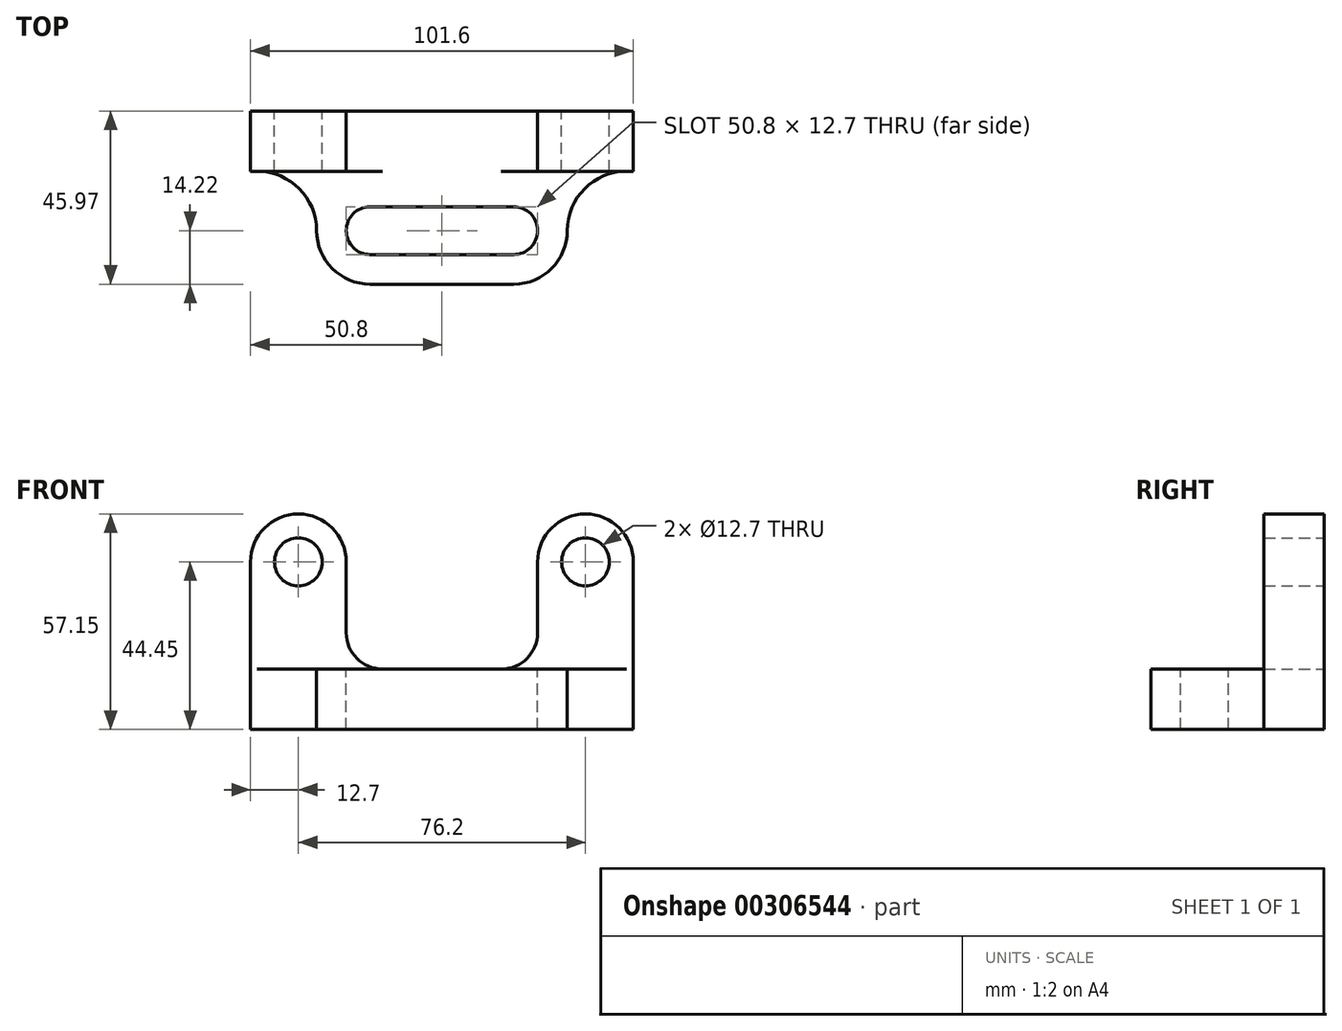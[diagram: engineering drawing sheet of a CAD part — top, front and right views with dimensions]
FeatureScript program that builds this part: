
annotation { "Feature Type Name" : "Feature", "Feature Type Description" : "" }
export const myFeature = defineFeature(function(context is Context, id is Id, definition is map)
    precondition{}
    {
        {
            var Q0;
            Q0=qCreatedBy(makeId("Front.planeOp"),FACE);
            var sketch = newSketch(context, id + "F0", { "sketchPlane" : qUnion([Q0])});
            skCircle(sketch, "E0", {"center": v(12.7, 44.45) * mm, "radius": 6.35 * mm});
            skCircle(sketch, "E1", {"center": v(88.9, 44.45) * mm, "radius": 6.35 * mm});
            skLineSegment(sketch, "E2", {"start": v(101.6, 44.45) * mm, "end": v(101.6, 0) * mm});
            skLineSegment(sketch, "E3", {"start": v(0, 44.45) * mm, "end": v(0, 0) * mm});
            skLineSegment(sketch, "E4", {"start": v(50.8, 0) * mm, "end": v(50.8, 24.18) * mm, "construction": true});
            skLineSegment(sketch, "E5", {"start": v(12.7, 44.45) * mm, "end": v(12.7, 34.07) * mm, "construction": true});
            skLineSegment(sketch, "E6", {"start": v(88.9, 44.45) * mm, "end": v(88.9, 31.32) * mm, "construction": true});
            skArc(sketch, "E7", {"start": v(0, 44.45) * mm, "mid": v(12.7, 57.15) * mm, "end": v(25.4, 44.45) * mm});
            skLineSegment(sketch, "E8", {"start": v(25.4, 44.45) * mm, "end": v(25.4, 25.65) * mm});
            skArc(sketch, "E9", {"start": v(25.4, 25.65) * mm, "mid": v(28.23, 18.83) * mm, "end": v(35.05, 16) * mm});
            skLineSegment(sketch, "E10", {"start": v(35.05, 16) * mm, "end": v(66.55, 16) * mm});
            skArc(sketch, "E11", {"start": v(66.55, 16) * mm, "mid": v(73.37, 18.83) * mm, "end": v(76.2, 25.65) * mm});
            skLineSegment(sketch, "E12", {"start": v(76.2, 25.65) * mm, "end": v(76.2, 44.45) * mm});
            skArc(sketch, "E13", {"start": v(101.6, 44.45) * mm, "mid": v(88.9, 57.15) * mm, "end": v(76.2, 44.45) * mm});
            skLineSegment(sketch, "E14", {"start": v(66.55, 16) * mm, "end": v(66.55, 22.94) * mm, "construction": true});
            skLineSegment(sketch, "E15", {"start": v(35.05, 16) * mm, "end": v(35.05, 31.62) * mm, "construction": true});
            skLineSegment(sketch, "E16", {"start": v(0, 0) * mm, "end": v(101.6, 0) * mm});
            skSolve(sketch);
        }
        {
            var Q0;
            Q0 = qSketchRegion(id + "F0", true);
            extrude(context, id + "F1", {"entities" : qUnion([Q0]), "depth" : 16 * mm});
        }
        {
            var Q0;
            Q0=makeQuery(id+"F1.opExtrude","CAP_FACE",FACE,{"disambiguationData":[OSD([sQuery(id+"F0.wireOp",EDGE,"E0"),sQuery(id+"F0.wireOp",EDGE,"E1"),sQuery(id+"F0.wireOp",EDGE,"E2"),sQuery(id+"F0.wireOp",EDGE,"E3"),sQuery(id+"F0.wireOp",EDGE,"E7"),sQuery(id+"F0.wireOp",EDGE,"E8"),sQuery(id+"F0.wireOp",EDGE,"E9"),sQuery(id+"F0.wireOp",EDGE,"E10"),sQuery(id+"F0.wireOp",EDGE,"E11"),sQuery(id+"F0.wireOp",EDGE,"E12"),sQuery(id+"F0.wireOp",EDGE,"E13"),sQuery(id+"F0.wireOp",EDGE,"E16")])],"isStart":false});
            var sketch = newSketch(context, id + "F2", { "sketchPlane" : qUnion([Q0])});
            skLineSegment(sketch, "E17.bottom", {"start": v(0, 0) * mm, "end": v(101.6, 0) * mm});
            skLineSegment(sketch, "E17.top", {"start": v(0, 16) * mm, "end": v(101.6, 16) * mm});
            skLineSegment(sketch, "E17.left", {"start": v(0, 0) * mm, "end": v(0, 16) * mm});
            skLineSegment(sketch, "E17.right", {"start": v(101.6, 0) * mm, "end": v(101.6, 16) * mm});
            skSolve(sketch);
        }
        {
            var Q0;
            Q0 = qSketchRegion(id + "F2", true);
            extrude(context, id + "F3", {"entities" : qUnion([Q0]), "operationType" : NewBodyOperationType.ADD, "depth" : 50.8 * mm});
        }
        {
            var Q0;
            Q0=makeQuery(id+"F3.boolean.opBoolean","MERGE",FACE,{"derivedFrom":[makeQuery(id+"F1.opExtrude","SWEPT_FACE",FACE,{"disambiguationData":[OSD([sQuery(id+"F0.wireOp",EDGE,"E10")])]}),makeQuery(id+"F3.opExtrude","SWEPT_FACE",FACE,{"disambiguationData":[OSD([sQuery(id+"F2.wireOp",EDGE,"E17.top")])]})]});
            var sketch = newSketch(context, id + "F4", { "sketchPlane" : qUnion([Q0])});
            skLineSegment(sketch, "E18", {"start": v(31.75, -31.75) * mm, "end": v(31.75, -19.05) * mm, "construction": true});
            skLineSegment(sketch, "E19", {"start": v(69.85, -31.75) * mm, "end": v(69.85, -21.92) * mm, "construction": true});
            skLineSegment(sketch, "E20", {"start": v(50.8, 0) * mm, "end": v(50.8, -10.67) * mm, "construction": true});
            skPoint(sketch, "E20.endSnap0", {"position": v(50.8, 0) * mm});
            skArc(sketch, "E21", {"start": v(17.53, -31.75) * mm, "mid": v(21.7, -41.8) * mm, "end": v(31.75, -45.97) * mm});
            skArc(sketch, "E22", {"start": v(84.07, -31.75) * mm, "mid": v(79.9, -41.8) * mm, "end": v(69.85, -45.97) * mm});
            skLineSegment(sketch, "E23", {"start": v(31.75, -45.97) * mm, "end": v(69.85, -45.97) * mm});
            skArc(sketch, "E24", {"start": v(17.53, -31.75) * mm, "mid": v(12.91, -20.61) * mm, "end": v(1.78, -16) * mm});
            skArc(sketch, "E25", {"start": v(84.07, -31.75) * mm, "mid": v(88.69, -20.61) * mm, "end": v(99.82, -16) * mm});
            skLineSegment(sketch, "E26", {"start": v(1.78, -16) * mm, "end": v(0, -16) * mm});
            skLineSegment(sketch, "E27", {"start": v(0, -16) * mm, "end": v(0, -66.8) * mm});
            skLineSegment(sketch, "E28", {"start": v(0, -66.8) * mm, "end": v(101.6, -66.8) * mm});
            skLineSegment(sketch, "E29", {"start": v(101.6, -66.8) * mm, "end": v(101.6, -16) * mm});
            skLineSegment(sketch, "E30", {"start": v(101.6, -16) * mm, "end": v(99.82, -16) * mm});
            skArc(sketch, "E31", {"start": v(31.75, -25.4) * mm, "mid": v(25.4, -31.75) * mm, "end": v(31.75, -38.1) * mm});
            skArc(sketch, "E32", {"start": v(69.85, -38.1) * mm, "mid": v(76.2, -31.75) * mm, "end": v(69.85, -25.4) * mm});
            skLineSegment(sketch, "E33", {"start": v(31.75, -25.4) * mm, "end": v(69.85, -25.4) * mm});
            skLineSegment(sketch, "E34", {"start": v(31.75, -38.1) * mm, "end": v(69.85, -38.1) * mm});
            skSolve(sketch);
        }
        {
            var Q0;
            Q0 = qSketchRegion(id + "F4", true);
            extrude(context, id + "F5", {"entities" : qUnion([Q0]), "operationType" : NewBodyOperationType.REMOVE, "endBound" : BoundingType.THROUGH_ALL, "oppositeDirection" : true, "depth" : 25.4 * mm});
        }
    });
